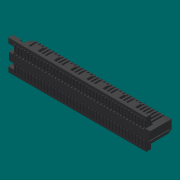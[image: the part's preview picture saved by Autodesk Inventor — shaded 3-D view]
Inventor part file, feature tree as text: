
AUTODESK INVENTOR PART (.ipt)
format: ipt  version: 2016 (Build 200138000, 138)  size: 1,159,168 bytes
history: native  units: mm
features: extrude x62, other x54, sketch x22, pattern_linear x2
ambient origin geometry x8: Origin, YZ Plane, XZ Plane, XY Plane, X Axis, Y Axis, Z Axis, Center Point
bodies: Solid1 (feature_tree)
feature tree (140):
  extrude  "Extrusion1"  Depth=0.94mm TaperAngle=0.0deg
  extrude  "Extrusion2"  Depth=16.83mm
  extrude  "Extrusion3"  Depth=5.0mm TaperAngle=0.0deg
  extrude  "Extrusion4"  Depth=16.25mm TaperAngle=0.0deg
  extrude  "Extrusion5"  Depth=1.2mm TaperAngle=0.0deg
  extrude  "Extrusion6"  Depth=1.2mm TaperAngle=0.0deg
  extrude  "Extrusion7"  Depth=1.2mm TaperAngle=0.0deg
  extrude  "Extrusion8"  Depth=0.4mm
  extrude  "Extrusion9"  Depth=3.0mm TaperAngle=0.0deg
  extrude  "Extrusion10"  Depth=3.0mm TaperAngle=0.0deg
  extrude  "Extrusion11"  Depth=3.0mm TaperAngle=0.0deg
  extrude  "Extrusion12"  Depth=3.0mm TaperAngle=0.0deg
  extrude  "Extrusion13"  Depth=3.0mm TaperAngle=0.0deg
  extrude  "Extrusion14"  Depth=3.0mm TaperAngle=0.0deg
  extrude  "Extrusion15"  Depth=3.0mm TaperAngle=0.0deg
  pattern_linear  "Rectangular Pattern1"  Spacing1=3.0mm  [1 undecoded]
  extrude  "Extrusion16"  Depth=3.0mm TaperAngle=0.0deg
  other  "Pattern_4_SKETCH_1"
  other  "Pattern_4_SKETCH_2"
  other  "Pattern_4_SKETCH_3"
  other  "Pattern_4_SKETCH_4"
  other  "Pattern_4_SKETCH_5"
  other  "Pattern_4_SKETCH_6"
  other  "Pattern_4_SKETCH_7"
  other  "Pattern_4_SKETCH_8"
  other  "Pattern_4_SKETCH_9"
  other  "Pattern_4_SKETCH_10"
  other  "Pattern_4_SKETCH_11"
  other  "Pattern_4_SKETCH_12"
  other  "Pattern_4_SKETCH_13"
  other  "Pattern_4_SKETCH_14"
  other  "Pattern_4_SKETCH_15"
  other  "Pattern_4_SKETCH_16"
  other  "Pattern_4_SKETCH_17"
  other  "Pattern_4_SKETCH_18"
  other  "Pattern_4_SKETCH_19"
  other  "Pattern_4_SKETCH_20"
  other  "Pattern_4_SKETCH_21"
  other  "Pattern_4_SKETCH_22"
  other  "Pattern_4_SKETCH_23"
  other  "Pattern_4_SKETCH_24"
  other  "Pattern_4_SKETCH_25"
  other  "Pattern_4_SKETCH_26"
  other  "Pattern_4_SKETCH_27"
  other  "Pattern_4_SKETCH_28"
  other  "Pattern_4_SKETCH_29"
  other  "Pattern_4_SKETCH_30"
  other  "Pattern_4_SKETCH_31"
  other  "Pattern_4_SKETCH_32"
  other  "Pattern_4_SKETCH_33"
  other  "Pattern_4_SKETCH_34"
  other  "Pattern_4_SKETCH_35"
  other  "Pattern_4_SKETCH_36"
  other  "Pattern_4_SKETCH_37"
  other  "Pattern_4_SKETCH_38"
  other  "Pattern_4_SKETCH_39"
  other  "Pattern_4_SKETCH_40"
  extrude  "Extrusion17"  Depth=3.0mm TaperAngle=0.0deg
  extrude  "Extrusion18"  Depth=3.0mm TaperAngle=0.0deg
  extrude  "Extrusion19"  Depth=3.0mm TaperAngle=0.0deg
  extrude  "Extrusion20"  Depth=3.0mm TaperAngle=0.0deg
  extrude  "Extrusion21"  Depth=3.0mm TaperAngle=0.0deg
  extrude  "Extrusion22"  Depth=3.0mm TaperAngle=0.0deg
  extrude  "Extrusion23"  Depth=3.0mm TaperAngle=0.0deg
  extrude  "Extrusion24"  Depth=3.0mm TaperAngle=0.0deg
  extrude  "Extrusion25"  Depth=3.0mm TaperAngle=0.0deg
  extrude  "Extrusion26"  Depth=3.0mm TaperAngle=0.0deg
  extrude  "Extrusion27"  Depth=3.0mm TaperAngle=0.0deg
  extrude  "Extrusion28"  Depth=3.0mm TaperAngle=0.0deg
  extrude  "Extrusion29"  Depth=3.0mm TaperAngle=0.0deg
  extrude  "Extrusion30"  Depth=3.0mm TaperAngle=0.0deg
  extrude  "Extrusion31"  Depth=3.0mm TaperAngle=0.0deg
  extrude  "Extrusion32"  Depth=3.0mm TaperAngle=0.0deg
  extrude  "Extrusion33"  Depth=3.0mm TaperAngle=0.0deg
  extrude  "Extrusion34"  Depth=3.0mm TaperAngle=0.0deg
  extrude  "Extrusion35"  Depth=2.8mm TaperAngle=0.0deg
  extrude  "Extrusion36"  Depth=2.8mm TaperAngle=0.0deg
  extrude  "Extrusion37"  Depth=1.325mm TaperAngle=0.0deg
  extrude  "Extrusion38"  Depth=2.0mm TaperAngle=0.0deg
  extrude  "Extrusion39"  Depth=0.05mm TaperAngle=0.0deg
  extrude  "Extrusion40"  Depth=2.8mm TaperAngle=0.0deg
  extrude  "Extrusion41"  Depth=2.8mm TaperAngle=0.0deg
  extrude  "Extrusion42"  [1 undecoded]
  extrude  "Extrusion43"  [1 undecoded]
  extrude  "Extrusion44"  [1 undecoded]
  extrude  "Extrusion45"  [1 undecoded]
  extrude  "Extrusion46"  [1 undecoded]
  extrude  "Extrusion47"  [1 undecoded]
  extrude  "Extrusion48"  [1 undecoded]
  extrude  "Extrusion49"  [1 undecoded]
  extrude  "Extrusion50"  [1 undecoded]
  extrude  "Extrusion51"  [1 undecoded]
  extrude  "Extrusion52"  [1 undecoded]
  extrude  "Extrusion53"  [1 undecoded]
  extrude  "Extrusion54"  [1 undecoded]
  extrude  "Extrusion55"  [1 undecoded]
  extrude  "Extrusion56"  [1 undecoded]
  extrude  "Extrusion57"  [1 undecoded]
  extrude  "Extrusion58"  [1 undecoded]
  extrude  "Extrusion59"  [1 undecoded]
  pattern_linear  "Rectangular Pattern2"  [2 undecoded]
  extrude  "Extrusion60"  [1 undecoded]
  extrude  "Extrusion61"  [1 undecoded]
  extrude  "Extrusion62"  [1 undecoded]
  other  "pin_XY"
  other  "pin_YZ"
  other  "pin_ZX"
  other  "pin_X"
  other  "pin_Y"
  other  "pin_Z"
  other  "pin_Center"
  other  "terminal_XY"
  other  "terminal_YZ"
  other  "terminal_ZX"
  other  "terminal_X"
  other  "terminal_Y"
  other  "terminal_Z"
  other  "terminal_Center"
  sketch  "Sketch_2"  dims[d4=16.83mm d5=0.0mm d6=0.51mm d7=-2.617994mm]
  sketch  "Sketch_1"  dims[d0=0.58mm d1=0.0mm d2=0.94mm d3=0.0mm]
  sketch  "Sketch_4"  dims[d12=13.25mm d13=0.0mm d14=16.25mm d15=0.0mm]
  sketch  "Sketch_3"  dims[d8=2.72mm d9=0.0mm d10=5.0mm d11=0.0mm]
  sketch  "Sketch_5"  dims[d16=1.2mm d17=0.0mm d18=1.2mm d19=0.0mm]
  sketch  "Sketch_6"  dims[d20=1.2mm d21=0.0mm d22=1.2mm d23=0.0mm]
  sketch  "Sketch_7"  dims[d24=1.2mm d25=0.0mm d26=1.2mm d27=0.0mm]
  sketch  "Sketch_8"  dims[d28=5.0mm d29=0.0mm d30=400.0mm d32=0.4mm d33=20.0mm d35=1.218mm]
  sketch  "Sketch_9"  dims[d36=3.0mm d37=0.0mm d38=3.0mm d39=0.0mm]
  sketch  "Sketch_10"  dims[d40=3.0mm d41=0.0mm d42=3.0mm d43=0.0mm]
  sketch  "Sketch_11"  dims[d44=3.0mm d45=0.0mm d46=3.0mm d47=0.0mm]
  sketch  "Sketch_12"  dims[d48=3.0mm d49=0.0mm d50=3.0mm d51=0.0mm]
  sketch  "Sketch_15"  dims[d52=3.0mm d53=0.0mm d54=3.0mm d55=0.0mm]
  sketch  "Sketch_16"  dims[d56=3.0mm d57=0.0mm d58=3.0mm d59=0.0mm]
  sketch  "Sketch_19"  dims[d60=3.0mm d61=0.0mm d62=3.0mm d63=0.0mm]
  sketch  "Sketch_21"  dims[d64=3.0mm d65=0.0mm]
  sketch  "Sketch_23"  dims[d66=3.0mm d67=0.0mm]
  sketch  "Sketch_25"  dims[d68=3.0mm d69=0.0mm]
  sketch  "Sketch_26"  dims[d70=3.0mm d71=0.0mm]
  sketch  "Sketch_28"  dims[d72=3.0mm d73=0.0mm]
  sketch  "Sketch_51"  dims[d74=3.0mm d75=0.0mm]
  sketch  "Sketch_52"  dims[d76=3.0mm d77=0.0mm d78=3.0mm d79=0.0mm d80=3.0mm d81=0.0mm d82=3.0mm d83=0.0mm d84=3.0mm d85=0.0mm d86=3.0mm d87=0.0mm d88=3.0mm d89=0.0mm d90=3.0mm d91=0.0mm d92=3.0mm d93=0.0mm d94=3.0mm d95=0.0mm d96=3.0mm d97=0.0mm d98=3.0mm d99=0.0mm d100=3.0mm d101=0.0mm d102=3.0mm d103=0.0mm d104=3.0mm d105=0.0mm d106=3.0mm d107=0.0mm d108=3.0mm d109=0.0mm d110=3.0mm d111=0.0mm d112=3.0mm d113=0.0mm d114=3.0mm d115=0.0mm d116=3.0mm d117=0.0mm d118=2.65mm d119=0.0mm d120=2.65mm d121=0.0mm d122=1.325mm d123=0.0mm d124=60.0mm d126=2.0mm d127=10.0mm d129=0.0mm d130=0.05mm d131=0.0mm d132=2.8mm d133=0.0mm d134=0.47mm d135=0.0mm]
note: 24 required parameter values undecoded (feature->parameter linkage not recoverable at this tier; creation-order binding heuristic only, values carry confidence <= 0.55)
